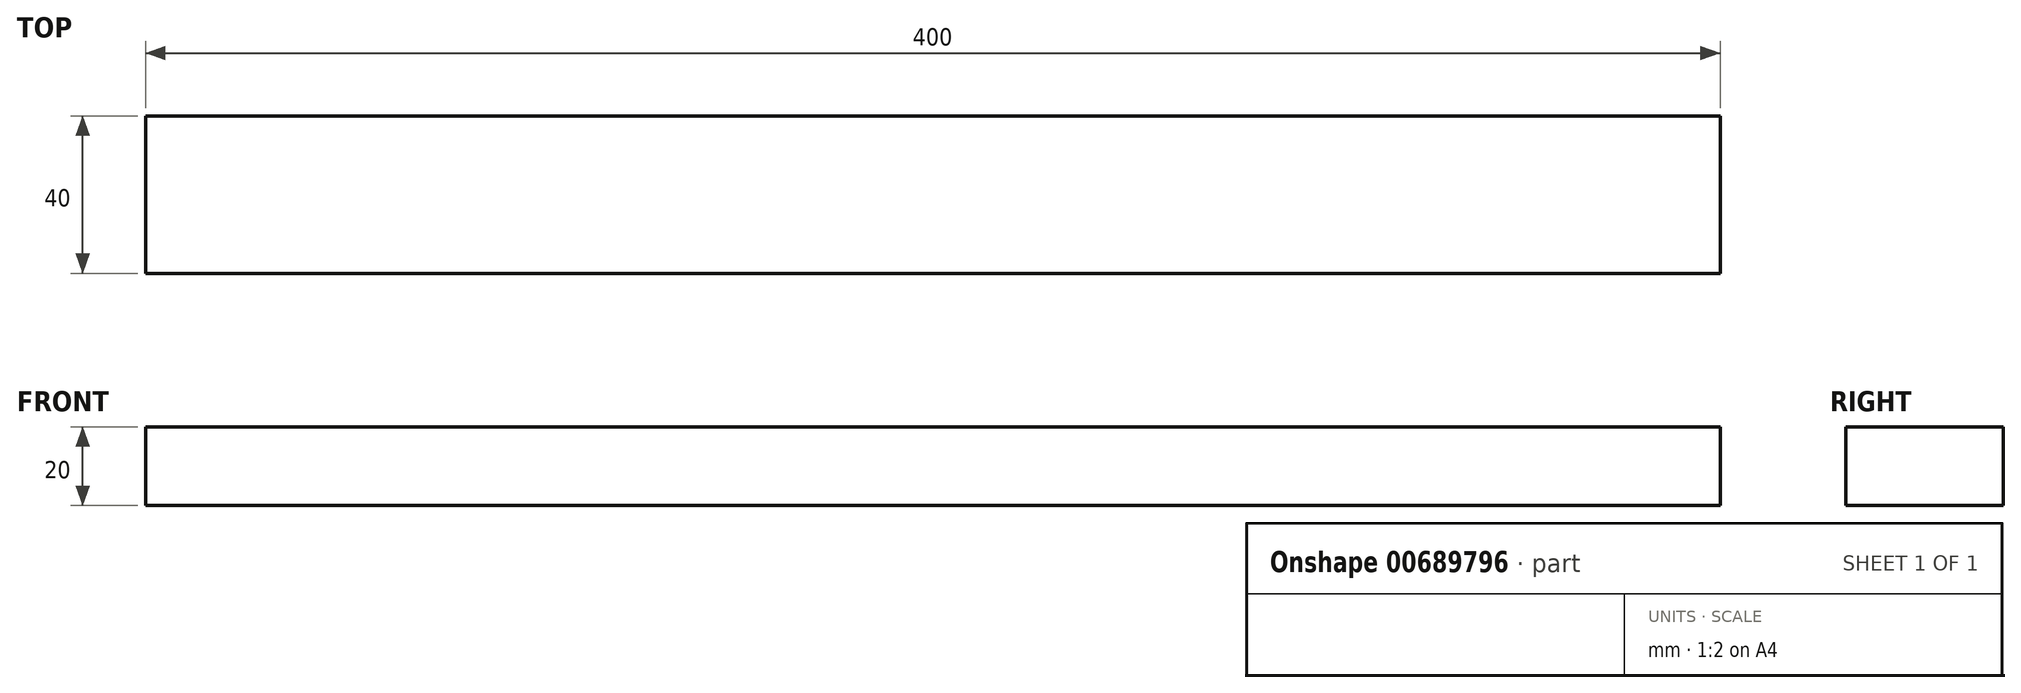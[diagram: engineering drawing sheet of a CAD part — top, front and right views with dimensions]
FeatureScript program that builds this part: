
annotation { "Feature Type Name" : "Feature", "Feature Type Description" : "" }
export const myFeature = defineFeature(function(context is Context, id is Id, definition is map)
    precondition{}
    {
        {
            var Q0;
            Q0=qCreatedBy(makeId("Right.planeOp"),FACE);
            var sketch = newSketch(context, id + "F0", { "sketchPlane" : qUnion([Q0])});
            skLineSegment(sketch, "E0.bottom", {"start": v(0, 0) * mm, "end": v(40, 0) * mm});
            skLineSegment(sketch, "E0.top", {"start": v(0, 20) * mm, "end": v(40, 20) * mm});
            skLineSegment(sketch, "E0.left", {"start": v(0, 0) * mm, "end": v(0, 20) * mm});
            skLineSegment(sketch, "E0.right", {"start": v(40, 0) * mm, "end": v(40, 20) * mm});
            skSolve(sketch);
        }
        {
            var Q0;
            Q0=makeQuery(id+"F0.imprint","IMPRINT",FACE,{"disambiguationData":[TD([[makeQuery(id+"F0.imprint","IMPRINT",EDGE,{"derivedFrom":sQuery(id+"F0.wireOp",EDGE,"E0.bottom")}),1.0]])]});
            extrude(context, id + "F1", {"entities" : qUnion([Q0]), "depth" : 400 * mm, "offsetDistance" : 25 * mm});
        }
    });
